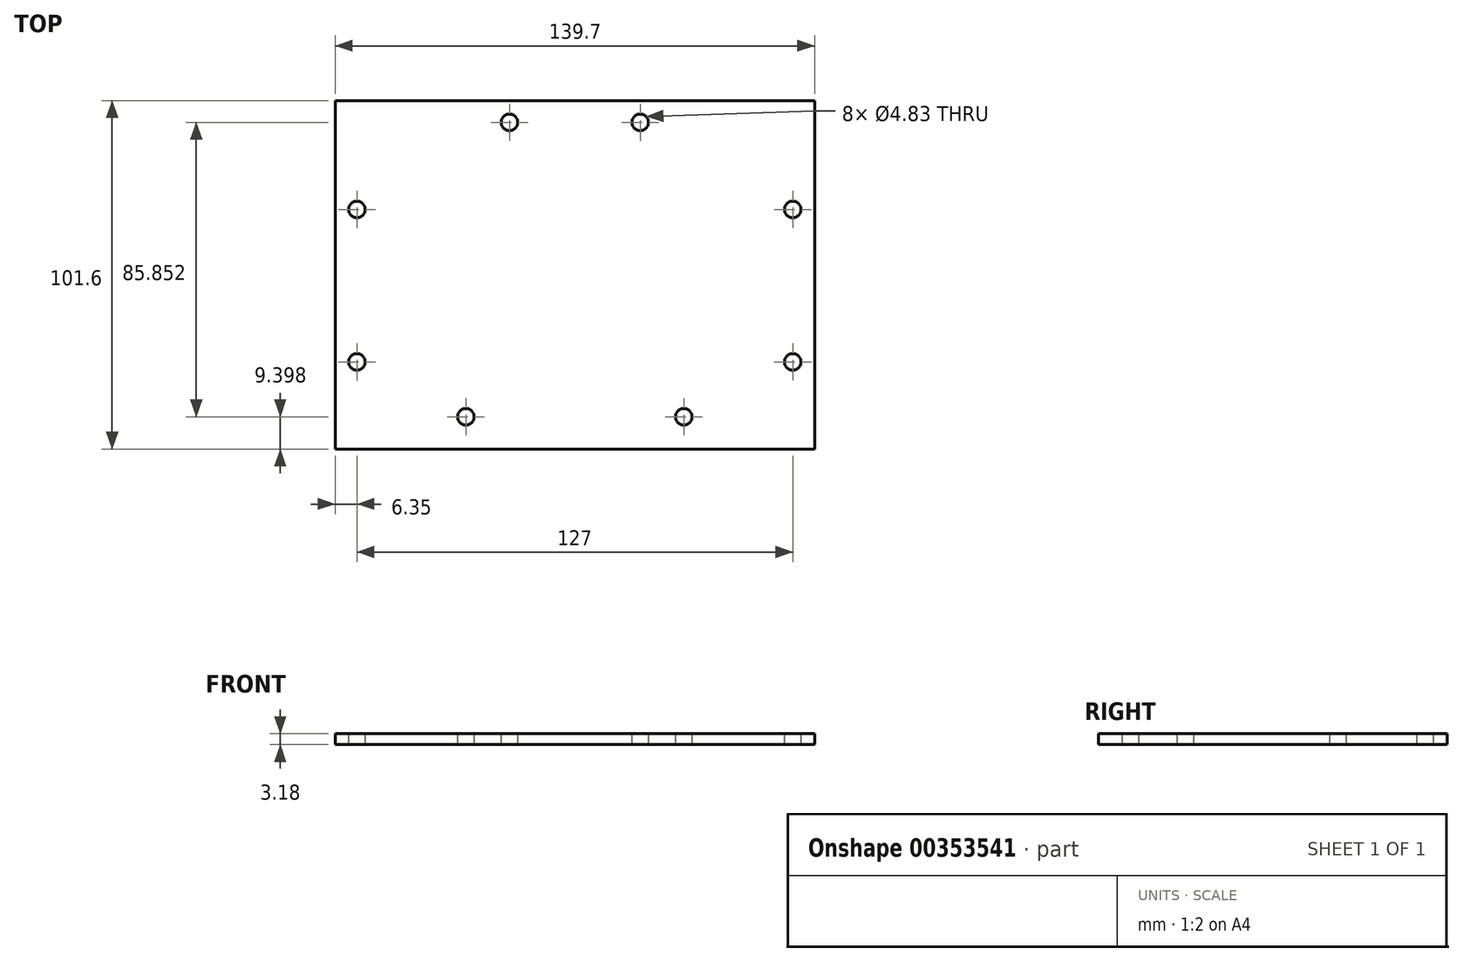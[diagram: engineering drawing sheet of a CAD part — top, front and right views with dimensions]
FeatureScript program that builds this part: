
annotation { "Feature Type Name" : "Feature", "Feature Type Description" : "" }
export const myFeature = defineFeature(function(context is Context, id is Id, definition is map)
    precondition{}
    {
        {
            var Q0;
            Q0=qCreatedBy(makeId("Top.planeOp"),FACE);
            var sketch = newSketch(context, id + "F0", { "sketchPlane" : qUnion([Q0])});
            skLineSegment(sketch, "E0.bottom", {"start": v(69.85, 50.8) * mm, "end": v(-69.85, 50.8) * mm});
            skLineSegment(sketch, "E0.top", {"start": v(69.85, -50.8) * mm, "end": v(-69.85, -50.8) * mm});
            skLineSegment(sketch, "E0.left", {"start": v(69.85, 50.8) * mm, "end": v(69.85, -50.8) * mm});
            skLineSegment(sketch, "E0.right", {"start": v(-69.85, 50.8) * mm, "end": v(-69.85, -50.8) * mm});
            skPoint(sketch, "E0.middle", {"position": v(0, 0) * mm});
            skSolve(sketch);
        }
        {
            var Q0;
            Q0 = qSketchRegion(id + "F0", true);
            extrude(context, id + "F1", {"entities" : qUnion([Q0]), "depth" : 3.17 * mm, "symmetric" : true});
        }
        {
            var Q0;
            Q0=makeQuery(id+"F1.opExtrude","CAP_FACE",FACE,{"disambiguationData":[OSD([sQuery(id+"F0.wireOp",EDGE,"E0.bottom"),sQuery(id+"F0.wireOp",EDGE,"E0.top"),sQuery(id+"F0.wireOp",EDGE,"E0.left"),sQuery(id+"F0.wireOp",EDGE,"E0.right")])],"isStart":false});
            var sketch = newSketch(context, id + "F2", { "sketchPlane" : qUnion([Q0])});
            skCircle(sketch, "E1", {"center": v(63.5, -25.4) * mm, "radius": 2.41 * mm});
            skCircle(sketch, "E2", {"center": v(63.5, 19.05) * mm, "radius": 2.41 * mm});
            skCircle(sketch, "E3", {"center": v(19.05, 44.45) * mm, "radius": 2.41 * mm});
            skCircle(sketch, "E4", {"center": v(-19.05, 44.45) * mm, "radius": 2.41 * mm});
            skCircle(sketch, "E5", {"center": v(-63.5, 19.05) * mm, "radius": 2.41 * mm});
            skCircle(sketch, "E6", {"center": v(-63.5, -25.4) * mm, "radius": 2.41 * mm});
            skCircle(sketch, "E7", {"center": v(-31.75, -41.4) * mm, "radius": 2.41 * mm});
            skCircle(sketch, "E8", {"center": v(31.75, -41.4) * mm, "radius": 2.41 * mm});
            skLineSegment(sketch, "E9", {"start": v(-19.05, 44.45) * mm, "end": v(-19.05, 50.8) * mm});
            skLineSegment(sketch, "E10", {"start": v(63.5, -25.4) * mm, "end": v(69.85, -25.4) * mm});
            skLineSegment(sketch, "E11", {"start": v(63.5, -25.4) * mm, "end": v(-69.85, -25.4) * mm});
            skLineSegment(sketch, "E12", {"start": v(63.5, 19.05) * mm, "end": v(63.5, 50.8) * mm});
            skSolve(sketch);
        }
        {
            var Q0;
            Q0 = qSketchRegion(id + "F2", true);
            extrude(context, id + "F3", {"entities" : qUnion([Q0]), "operationType" : NewBodyOperationType.REMOVE, "oppositeDirection" : true, "depth" : 25.4 * mm});
        }
    });
